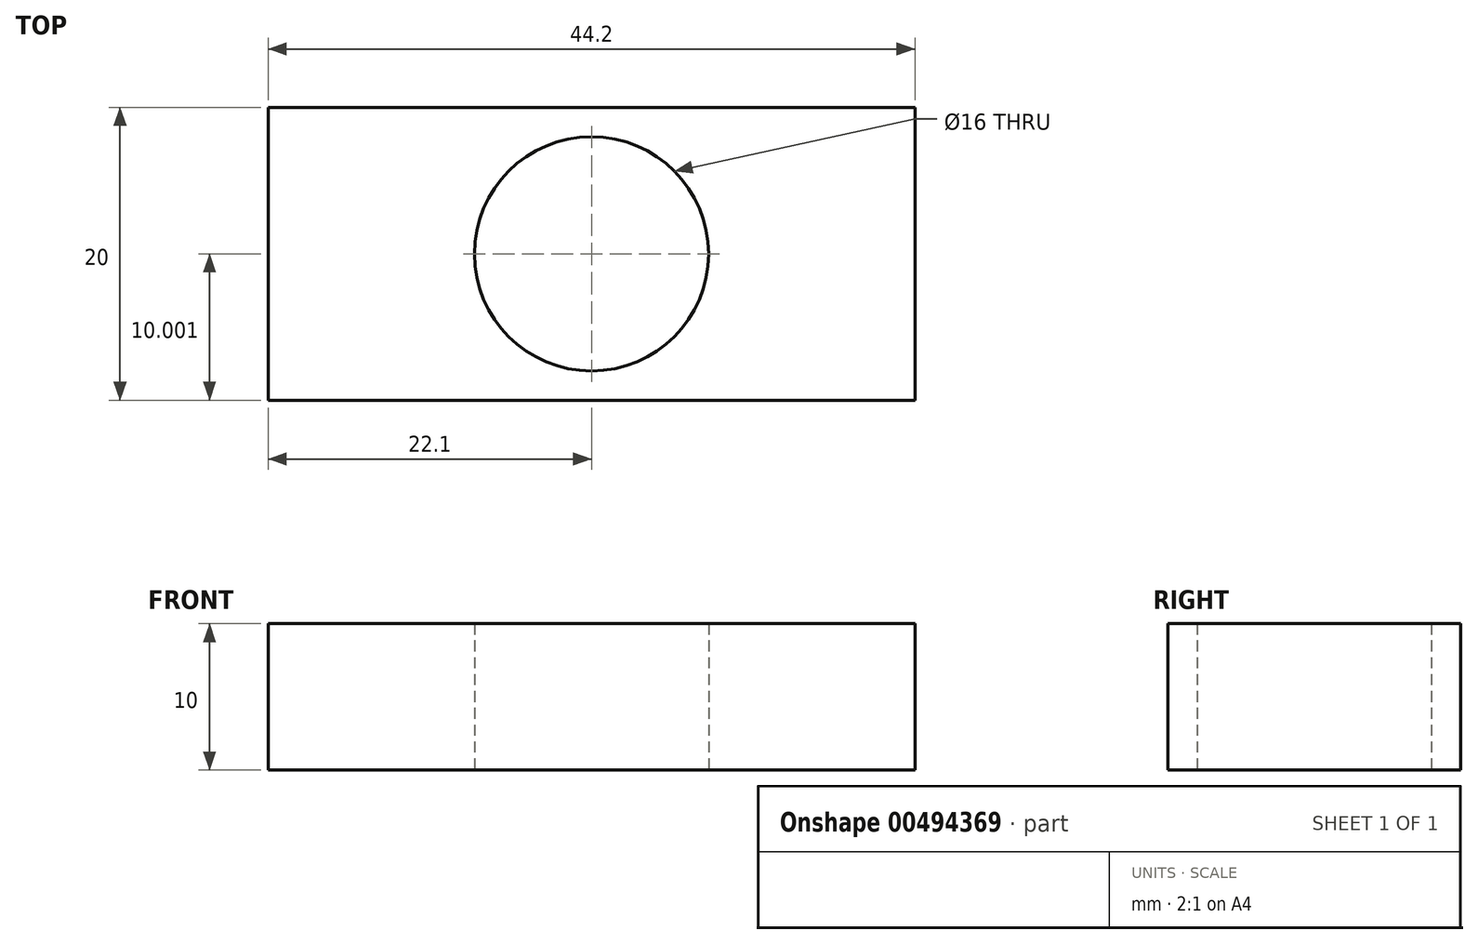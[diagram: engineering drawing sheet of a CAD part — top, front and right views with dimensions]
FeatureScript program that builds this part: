
annotation { "Feature Type Name" : "Feature", "Feature Type Description" : "" }
export const myFeature = defineFeature(function(context is Context, id is Id, definition is map)
    precondition{}
    {
        {
            var Q0;
            Q0=qCreatedBy(makeId("Top.planeOp"),FACE);
            var sketch = newSketch(context, id + "F0", { "sketchPlane" : qUnion([Q0])});
            skLineSegment(sketch, "E0.bottom", {"start": v(-22.1, 6.95) * mm, "end": v(22.1, 6.95) * mm});
            skLineSegment(sketch, "E0.top", {"start": v(-22.1, -13.05) * mm, "end": v(22.1, -13.05) * mm});
            skLineSegment(sketch, "E0.left", {"start": v(-22.1, 6.95) * mm, "end": v(-22.1, -13.05) * mm});
            skLineSegment(sketch, "E0.right", {"start": v(22.1, 6.95) * mm, "end": v(22.1, -13.05) * mm});
            skCircle(sketch, "E1", {"center": v(0, -3.05) * mm, "radius": 8 * mm});
            skPoint(sketch, "E1.centerSnap0", {"position": v(0, -13.05) * mm});
            skLineSegment(sketch, "E2", {"start": v(-22.1, 6.95) * mm, "end": v(22.1, -13.05) * mm});
            skLineSegment(sketch, "E3", {"start": v(22.1, 6.95) * mm, "end": v(-22.1, -13.05) * mm});
            skSolve(sketch);
        }
        {
            var Q0;
            Q0 = qSketchRegion(id + "F0", true);
            extrude(context, id + "F1", {"entities" : qUnion([Q0]), "depth" : 10 * mm, "offsetDistance" : 25.4 * mm});
        }
    });
